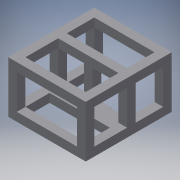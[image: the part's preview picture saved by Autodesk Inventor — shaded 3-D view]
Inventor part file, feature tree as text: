
AUTODESK INVENTOR PART (.ipt)
format: ipt  version: 2018 (Build 220112000, 112)  size: 221,184 bytes
history: native  units: mm
features: extrude x5, sketch x5, projected_geometry x2, other x2, reference x1
ambient origin geometry x8: Origin, YZ Plane, XZ Plane, XY Plane, X Axis, Y Axis, Z Axis, Center Point
bodies: Solid1 (feature_tree)
feature tree (15):
  extrude  "Extrusion1"  Depth=400.0mm
  extrude  "Extrusion2"  Depth=400.0mm
  extrude  "Extrusion3"  Depth=15.0mm
  extrude  "Extrusion4"  Depth=40.0mm TaperAngle=0.0deg
  extrude  "Extrusion5"  Depth=44.0mm
  sketch  "Sketch1"  dims[d0=40.0mm d1=400.0mm]
  reference  "Reference1"
  sketch  "Sketch2"  dims[d2=40.0mm d3=400.0mm]
  projected_geometry  "Projected Loop1"
  sketch  "Sketch3"  dims[d4=15.0mm d5=15.0mm]
  projected_geometry  "Projected Loop2"
  sketch  "Sketch4"  dims[d6=40.0mm d7=40.0mm d8=0.0mm]
  sketch  "Sketch5"  dims[d9=80.0mm d10=44.0mm d11=44.0mm d12=118.0mm d13=118.0mm d14=44.0mm d15=0.0mm d16=5.0mm d17=20.0mm d18=0.0mm d21=20.0mm d22=40.0mm d23=40.0mm d24=200.0mm d25=0.0mm d26=40.0mm d27=0.0mm d28=40.0mm d29=40.0mm d30=40.0mm d31=40.0mm]
  other  "Assembly1"
  other  "BSF_Accelerator_v01:1"
